# Revit family: 303_R432_
name_source: partatom
category: Pipe Accessories
revit_build: Autodesk Revit 2018 (Build: 20170223_1515(x64)
units: mm (PartAtom-declared; Revit-internal decimal feet)

## family parameters
Always vertical = Yes
Cut with Voids When Loaded = No
Part Type = Valve - Breaks Into
Round Connector Dimension = Use Diameter
Shared = No
Work Plane-Based = No

## types (3) — shared parameters
B4 = 6 mm  [stored 0.019685 ft]
CAT0 = Yes
CenSd_W2_6 = 13 mm
Description = Micrometric straight valve with thermostatic option
J6 = 49 mm  [stored 0.160761 ft]
L2 = 9 mm  [stored 0.0295276 ft]
L2D_Min = 3048 mm  [stored 10 ft]
L5 = 4 mm  [stored 0.0131234 ft]
L6 = 4 mm  [stored 0.0131234 ft]
L62 = 2 mm  [stored 0.00656168 ft]
L62__ve = -2 mm  [stored -0.00656168 ft]
L6__ve = -4 mm  [stored -0.0131234 ft]
L8 = 2 mm  [stored 0.00656168 ft]
L8__ve = -2 mm  [stored -0.00656168 ft]
LC = 51 mm  [stored 0.167323 ft]
M1 = 21 mm  [stored 0.0688976 ft]
Manufacturer = Giacomini
QmdConnectorList = 301;D;302;D
URL = http://www.giacomini.com
W2 = 15 mm  [stored 0.0492126 ft]
W4 = 11 mm
X11 = 13 mm
magiPartTypeId = 303
magiProductFamilyId = R432*
zero-valued in all types: MC_Default_elevation

## per-type parameters (varying)
| type | B3 | D | G3 | K3 | L2D | LC1 | LC2 | LX | R1 | W2D |
| R432X032 | 9 mm  [stored 0.0295276 ft] | 16 mm | 10 mm  [stored 0.0328084 ft] | 9 mm  [stored 0.0295276 ft] | 56 mm | 28 mm  [stored 0.0918635 ft] | 37 mm | 34 mm | 8 mm  [stored 0.0262467 ft] | 16 mm  [stored 0.0524934 ft] |
| R432X034 | 10 mm  [stored 0.0328084 ft] | 18 mm | 12 mm  [stored 0.0393701 ft] | 10 mm  [stored 0.0328084 ft] | 57 mm | 29 mm | 38 mm | 35 mm | 11 mm | 18 mm  [stored 0.0590551 ft] |
| R432X033 | 9 mm  [stored 0.0295276 ft] | 16 mm | 12 mm  [stored 0.0393701 ft] | 9 mm  [stored 0.0295276 ft] | 56 mm | 28 mm  [stored 0.0918635 ft] | 37 mm | 34 mm | 11 mm | 16 mm  [stored 0.0524934 ft] |

note: column(s) folded — value = type name in every type: magiProductCode, magiProductId

note: [stored X ft] marks values corroborated as IEEE doubles in the binary element streams (Revit-internal decimal feet)

## geometry (parser evidence)
native form markers: Sweep x1
no freeform markers — native parametric forms only
